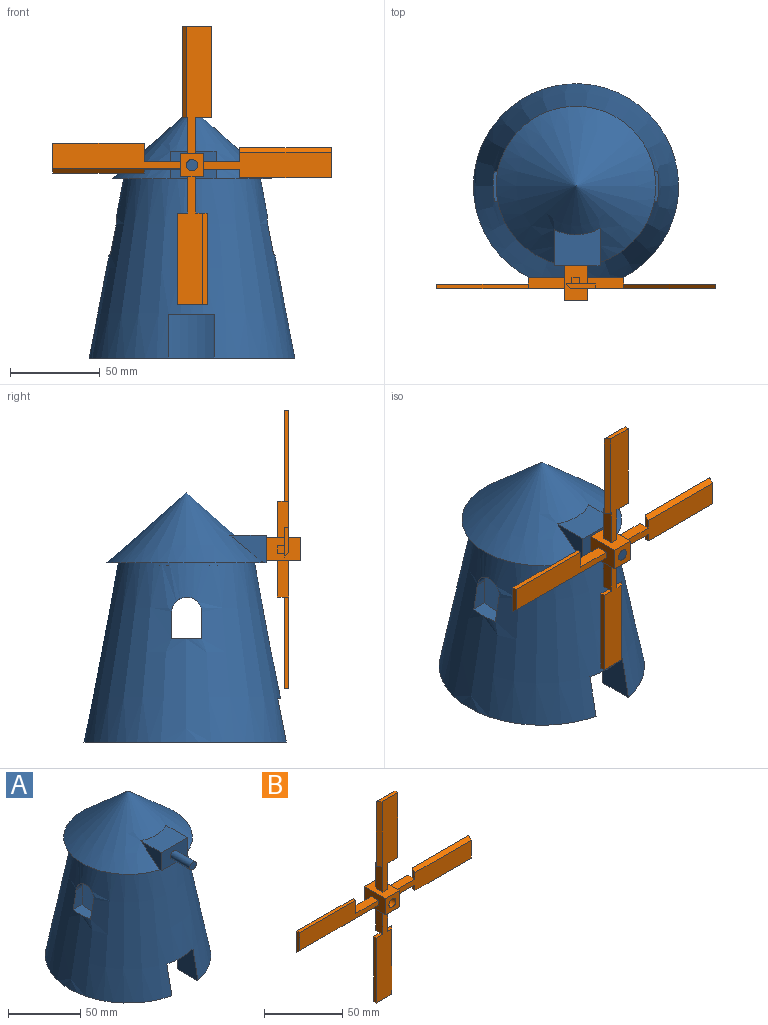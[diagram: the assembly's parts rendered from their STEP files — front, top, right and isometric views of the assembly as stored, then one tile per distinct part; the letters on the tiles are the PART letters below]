
ASSEMBLY  parts=2 mates=1
PART A: 23 faces, bbox 114.3x120.7x139 mm
  f0: cone r=44.45mm half-angle=48.6deg, axis (0,0,-1), area 7670.4mm2, adj f3,f9,f10,f11
  f1: plane 114.3x112.92mm, normal (0,0,-1), area 5295.8mm2, adj f2,f5,f6,f7
  f2: cone r=38.1mm half-angle=10.8deg, axis (0,0,-1), area 29020.1mm2, adj f1,f3,f4,f5,f6,f15,f16,f17
  f3: plane 88.9x88.9mm, normal (0,0,-1), area 1662.5mm2, adj f0,f2,f9,f10,f12
  f4: plane 25.4x17.07mm, normal (0,0,-1), area 380.7mm2, adj f2,f5,f6,f7
  f5: plane 24.53x20.25mm, normal (-1,0,0), area 435.8mm2, adj f1,f2,f4,f7
  f6: plane 24.53x20.31mm, normal (1,0,0), area 437.2mm2, adj f1,f2,f4,f7
  f7: cylinder r=37.7mm len=98.04mm, axis (0,0,-1), area 21858mm2, adj f1,f4,f5,f6,f8,f15,f16,f17
  f8: plane 75.39x75.39mm, normal (0,0,-1), area 4464.5mm2, adj f7
  f9: plane 20.11x15.24mm, normal (-1,0,0), area 164.3mm2, adj f0,f3,f11,f12
  f10: plane 20.84x15.24mm, normal (1,0,0), area 172.5mm2, adj f0,f3,f11,f12
  f11: plane 25.4x20.84mm, normal (0,0,1), area 465.9mm2, adj f0,f9,f10,f12
  f12: plane 25.4x15.24mm, normal (0,-1,0), area 355.4mm2, adj f3,f9,f10,f11,f13
  f13: cylinder r=3.17mm len=19.05mm, axis (0,1,0), area 380mm2, adj f12,f14
  f14: plane 6.35x6.35mm, normal (0,-1,0), area 31.7mm2, adj f13
  f15: plane 16.88x9.52mm, normal (0,0,1), area 144.4mm2, adj f2,f7,f16,f18
  f16: plane 14.86x8.71mm, normal (0,1,0), area 107.6mm2, adj f2,f7,f15,f17
  f17: cylinder r=8.44mm len=16.88mm, axis (1,0,0), area 128.6mm2, adj f2,f7,f16,f18
  f18: plane 15.15x8.68mm, normal (0,-1,0), area 108.9mm2, adj f2,f7,f15,f17
  f19: plane 15.15x8.68mm, normal (0,-1,0), area 108.9mm2, adj f2,f7,f20,f22
  f20: cylinder r=8.44mm len=16.88mm, axis (1,0,0), area 122.9mm2, adj f2,f7,f19,f21
  f21: plane 14.86x8.71mm, normal (0,1,0), area 107.6mm2, adj f2,f7,f20,f22
  f22: plane 16.88x9.52mm, normal (0,0,1), area 144.4mm2, adj f2,f7,f19,f21
PART B: 51 faces, bbox 154.9x19.1x155 mm
  f0: plane 4.32x3.81mm, normal (0,0,-1), area 16.5mm2, adj f14,f15,f16,f46
  f1: plane 4.32x3.81mm, normal (0,0,1), area 16.5mm2, adj f23,f24,f25,f41
  f2: plane 19.05x12.7mm, normal (0,0,-1), area 214.5mm2, adj f3,f6,f7,f8,f14,f15,f16,f17
  f3: plane 19.05x12.7mm, normal (1,0,0), area 214.5mm2, adj f2,f4,f7,f8,f19,f20,f21,f22
  f4: plane 19.05x12.7mm, normal (0,0,1), area 214.5mm2, adj f3,f6,f7,f8,f23,f24,f25,f26
  f5: cylinder r=3.17mm len=19.05mm, axis (0,1,0), area 380mm2, adj f7,f8
  f6: plane 19.05x12.7mm, normal (-1,0,0), area 214.6mm2, adj f2,f4,f7,f8,f9,f11,f12,f13
  f7: plane 12.7x12.7mm, normal (0,-1,0), area 129.6mm2, adj f2,f3,f4,f5,f6
  f8: plane 12.7x12.7mm, normal (0,1,0), area 129.6mm2, adj f2,f3,f4,f5,f6
  f9: plane 20.32x6.35mm, normal (0,0,1), area 129mm2, adj f6,f10,f12,f13,f32
  f10: plane 4.32x3.81mm, normal (-1,0,0), area 16.5mm2, adj f9,f11,f12,f36
  f11: plane 20.32x5.78mm, normal (0,0,-1), area 117.5mm2, adj f6,f10,f12,f33,f50
  f12: plane 20.32x4.32mm, normal (0,1,0), area 87.9mm2, adj f6,f9,f10,f11
  f13: plane 71.12x13.97mm, normal (0,-1,0), area 786mm2, adj f6,f9,f32,f34,f35,f50
  f14: plane 20.32x6.35mm, normal (-1,0,0), area 129mm2, adj f0,f2,f16,f17,f42
  f15: plane 20.32x6.35mm, normal (1,0,0), area 129mm2, adj f0,f2,f16,f17,f43
  f16: plane 20.32x4.32mm, normal (0,1,0), area 87.7mm2, adj f0,f2,f14,f15
  f17: plane 71.14x13.97mm, normal (0,-1,0), area 797.7mm2, adj f2,f14,f15,f42,f43,f44,f45,f49
  f18: plane 4.32x3.81mm, normal (1,0,0), area 16.5mm2, adj f19,f20,f21,f31
  f19: plane 20.32x6.35mm, normal (0,0,1), area 129mm2, adj f3,f18,f21,f22,f28
  f20: plane 20.32x6.35mm, normal (0,0,-1), area 129mm2, adj f3,f18,f21,f22,f27
  f21: plane 20.32x4.32mm, normal (0,1,0), area 87.9mm2, adj f3,f18,f19,f20
  f22: plane 71.12x13.97mm, normal (0,-1,0), area 797.5mm2, adj f3,f19,f20,f27,f28,f29,f30,f48
  f23: plane 20.32x6.35mm, normal (1,0,0), area 129mm2, adj f1,f4,f25,f26,f38
  f24: plane 20.32x6.35mm, normal (-1,0,0), area 129mm2, adj f1,f4,f25,f26,f37
  f25: plane 20.32x4.32mm, normal (0,1,0), area 87.7mm2, adj f1,f4,f23,f24
  f26: plane 71.12x13.97mm, normal (0,-1,0), area 797.4mm2, adj f4,f23,f24,f37,f38,f39,f40,f47
  f27: plane 4.51x2.54mm, normal (-1,0,0), area 11.5mm2, adj f20,f22,f29,f31
  f28: plane 7.68x2.54mm, normal (-1,0,0), area 16.3mm2, adj f19,f22,f31,f48
  f29: plane 50.8x2.54mm, normal (0,0,-1), area 129mm2, adj f22,f27,f30,f31
  f30: plane 16.51x2.54mm, normal (1,0,0), area 38.7mm2, adj f22,f29,f31,f48
  f31: plane 50.8x16.51mm, normal (0,1,0), area 838.7mm2, adj f18,f27,f28,f29,f30,f48
  f32: plane 10.22x2.54mm, normal (1,0,0), area 25.9mm2, adj f9,f13,f34,f36
  f33: plane 1.97x1.97mm, normal (1,0,0), area 1.9mm2, adj f11,f36,f50
  f34: plane 50.8x2.54mm, normal (0,0,1), area 129mm2, adj f13,f32,f35,f36
  f35: plane 16.51x2.54mm, normal (-1,0,0), area 38.7mm2, adj f13,f34,f36,f50
  f36: plane 50.8x16.51mm, normal (0,1,0), area 838.7mm2, adj f10,f32,f33,f34,f35,f50
  f37: plane 3.26x2.54mm, normal (0,0,-1), area 5mm2, adj f24,f26,f41,f47
  f38: plane 8.93x2.54mm, normal (0,0,-1), area 22.7mm2, adj f23,f26,f39,f41
  f39: plane 50.8x2.54mm, normal (1,0,0), area 129mm2, adj f26,f38,f40,f41
  f40: plane 16.51x2.54mm, normal (0,0,1), area 38.7mm2, adj f26,f39,f41,f47
  f41: plane 50.8x16.51mm, normal (0,1,0), area 838.7mm2, adj f1,f37,f38,f39,f40,f47
  f42: plane 5.8x2.54mm, normal (0,0,1), area 14.7mm2, adj f14,f17,f44,f46
  f43: plane 6.39x2.54mm, normal (0,0,1), area 13mm2, adj f15,f17,f46,f49
  f44: plane 50.82x2.54mm, normal (-1,0,0), area 129.1mm2, adj f17,f42,f45,f46
  f45: plane 16.51x2.54mm, normal (0,0,-1), area 38.7mm2, adj f17,f44,f46,f49
  f46: plane 50.82x16.51mm, normal (0,1,0), area 839mm2, adj f0,f42,f43,f44,f45,f49
  f47: plane 50.8x2.54mm, normal (-0.71,-0.71,0), area 182.5mm2, adj f26,f37,f40,f41
  f48: plane 50.8x2.54mm, normal (0,-0.71,0.71), area 182.5mm2, adj f22,f28,f30,f31
  f49: plane 50.82x2.54mm, normal (0.71,-0.71,0), area 182.6mm2, adj f17,f43,f45,f46
  f50: plane 71.12x2.54mm, normal (0,-0.71,-0.71), area 198.8mm2, adj f6,f11,f13,f33,f35,f36
PLACE A t=(-78.9,-64.35,7.42)mm
PLACE B t=(-89.6,-121.5,56.63)mm
MATE revolute B.f5 <-> A.f13  axis (0,-1,0) through (-78.9,-127.85,53.78)mm
